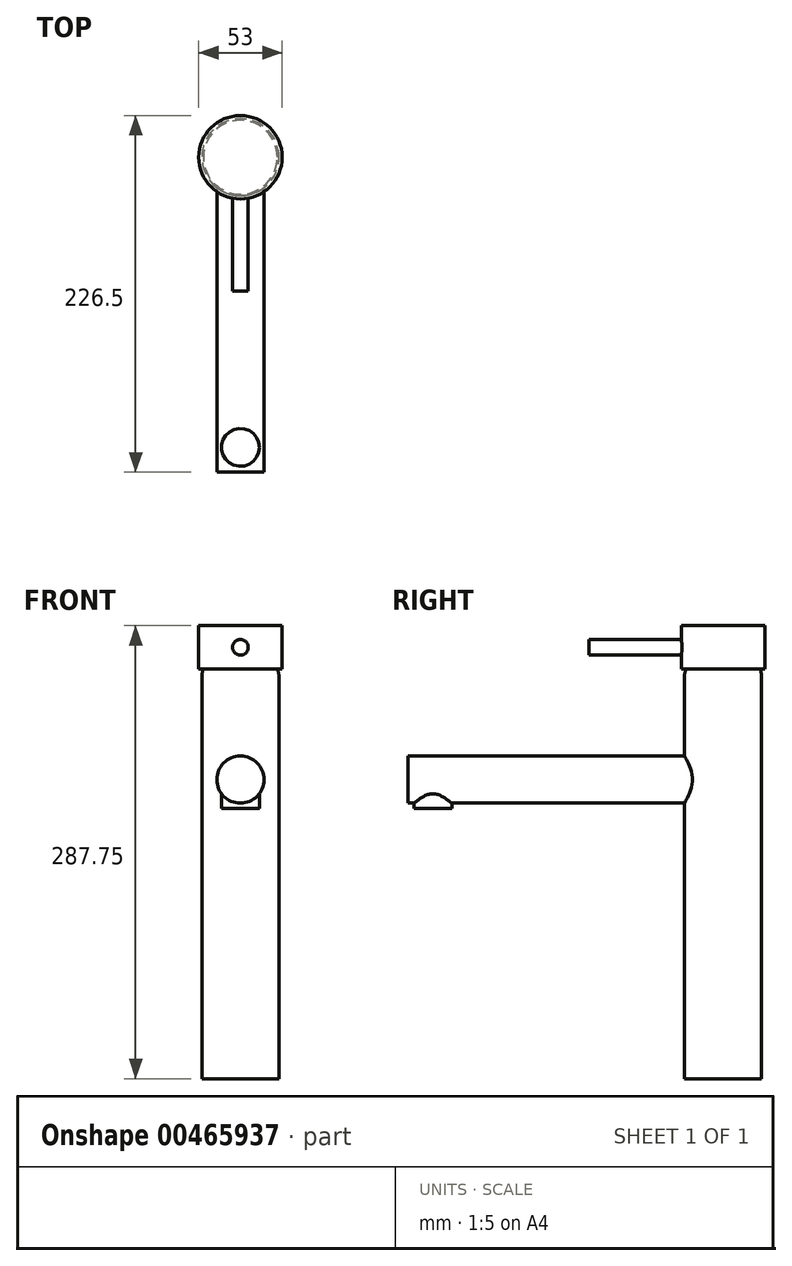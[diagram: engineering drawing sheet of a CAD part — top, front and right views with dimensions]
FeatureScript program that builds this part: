
annotation { "Feature Type Name" : "Feature", "Feature Type Description" : "" }
export const myFeature = defineFeature(function(context is Context, id is Id, definition is map)
    precondition{}
    {
        {
            var Q0;
            Q0=qCreatedBy(makeId("Top.planeOp"),FACE);
            var sketch = newSketch(context, id + "F0", { "sketchPlane" : qUnion([Q0])});
            skCircle(sketch, "E0", {"center": v(0, 0) * mm, "radius": 24.5 * mm});
            skSolve(sketch);
        }
        {
            var Q0;
            Q0 = qSketchRegion(id + "F0", true);
            extrude(context, id + "F1", {"entities" : qUnion([Q0]), "depth" : 255 * mm});
        }
        {
            var Q0;
            Q0=makeQuery(id+"F1.opExtrude","CAP_FACE",FACE,{"disambiguationData":[OSD([sQuery(id+"F0.wireOp",EDGE,"E0")])],"isStart":false});
            var sketch = newSketch(context, id + "F2", { "sketchPlane" : qUnion([Q0])});
            skCircle(sketch, "E1", {"center": v(0, 0) * mm, "radius": 24.5 * mm});
            skSolve(sketch);
        }
        {
            var Q0;
            Q0 = qSketchRegion(id + "F2", true);
            extrude(context, id + "F3", {"entities" : qUnion([Q0]), "operationType" : NewBodyOperationType.ADD, "depth" : 14 * mm});
        }
        {
            var Q0;
            Q0=makeQuery(id+"F3.opExtrude","CAP_EDGE",EDGE,{"disambiguationData":[OSD([sQuery(id+"F2.wireOp",EDGE,"E1")])],"isStart":false});
            fillet(context, id + "F4", {"entities" : qUnion([Q0]), "radius" : 14 * mm, "tangentPropagation" : true, "allowEdgeOverflow" : false});
        }
        {
            var Q0;
            Q0=qCreatedBy(makeId("Top.planeOp"),FACE);
            cPlane(context, id + "F5", {"entities" : qUnion([Q0]), "cplaneType" : CPlaneType.OFFSET, "offset" : 274 * mm, "width" : 150 * mm, "height" : 150 * mm});
        }
        {
            var Q0;
            Q0=qCreatedBy(id+"F5.planeOp",FACE);
            var sketch = newSketch(context, id + "F6", { "sketchPlane" : qUnion([Q0])});
            skCircle(sketch, "E2", {"center": v(0, 0) * mm, "radius": 26.5 * mm});
            skSolve(sketch);
        }
        {
            var Q0;
            Q0 = qSketchRegion(id + "F6", true);
            extrude(context, id + "F7", {"entities" : qUnion([Q0]), "operationType" : NewBodyOperationType.ADD, "endBound" : BoundingType.SYMMETRIC, "depth" : 27.5 * mm});
        }
        {
            var Q0;
            Q0=qCreatedBy(makeId("Front.planeOp"),FACE);
            var sketch = newSketch(context, id + "F8", { "sketchPlane" : qUnion([Q0])});
            skLineSegment(sketch, "E3", {"start": v(0, 0) * mm, "end": v(0, 318.76) * mm, "construction": true});
            skCircle(sketch, "E4", {"center": v(0, 274) * mm, "radius": 5 * mm});
            skSolve(sketch);
        }
        {
            var Q0;
            Q0 = qSketchRegion(id + "F8", true);
            extrude(context, id + "F9", {"entities" : qUnion([Q0]), "operationType" : NewBodyOperationType.ADD, "depth" : 85 * mm});
        }
        {
            var Q0;
            Q0=qCreatedBy(makeId("Front.planeOp"),FACE);
            var sketch = newSketch(context, id + "F10", { "sketchPlane" : qUnion([Q0])});
            skLineSegment(sketch, "E5", {"start": v(0, 0) * mm, "end": v(0, 324.57) * mm, "construction": true});
            skCircle(sketch, "E6", {"center": v(0, 190) * mm, "radius": 15 * mm});
            skSolve(sketch);
        }
        {
            var Q0;
            Q0 = qSketchRegion(id + "F10", true);
            extrude(context, id + "F11", {"entities" : qUnion([Q0]), "operationType" : NewBodyOperationType.ADD, "depth" : 200 * mm});
        }
        {
            var Q0;
            Q0=qCreatedBy(makeId("Top.planeOp"),FACE);
            cPlane(context, id + "F12", {"entities" : qUnion([Q0]), "cplaneType" : CPlaneType.OFFSET, "offset" : 190 * mm, "width" : 150 * mm, "height" : 150 * mm});
        }
        {
            var Q0;
            Q0=qCreatedBy(id+"F12.planeOp",FACE);
            var sketch = newSketch(context, id + "F13", { "sketchPlane" : qUnion([Q0])});
            skLineSegment(sketch, "E7", {"start": v(0, 0) * mm, "end": v(0, -216.25) * mm, "construction": true});
            skCircle(sketch, "E8", {"center": v(0, -184.25) * mm, "radius": 12 * mm});
            skSolve(sketch);
        }
        {
            var Q0;
            Q0 = qSketchRegion(id + "F13", true);
            extrude(context, id + "F14", {"entities" : qUnion([Q0]), "operationType" : NewBodyOperationType.ADD, "oppositeDirection" : true, "depth" : 18.5 * mm});
        }
    });
